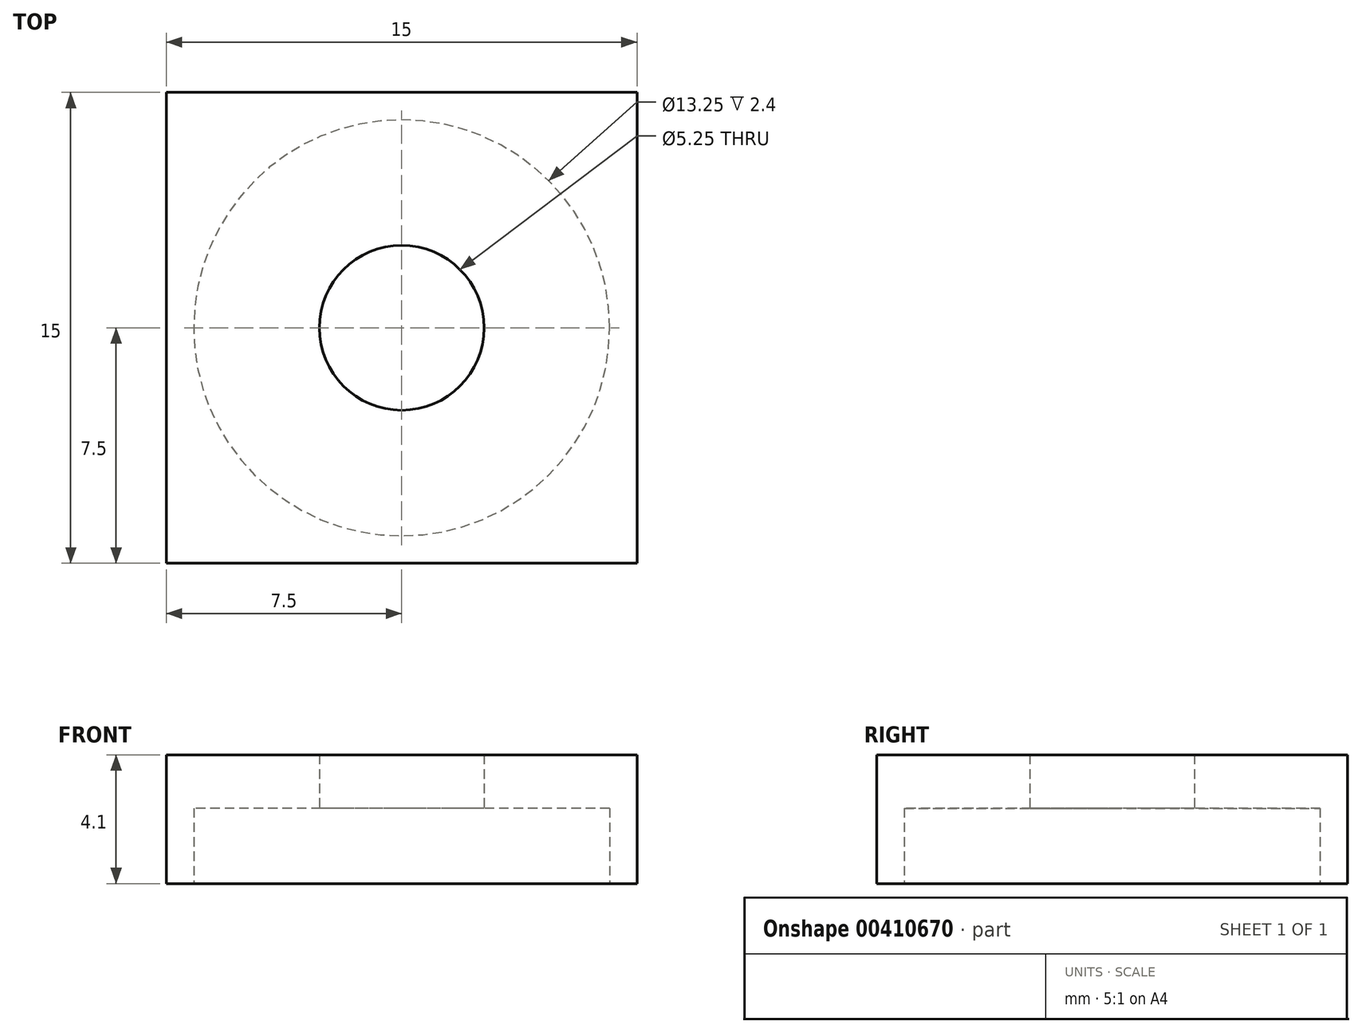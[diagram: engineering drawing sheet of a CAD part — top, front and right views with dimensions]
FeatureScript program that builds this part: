
annotation { "Feature Type Name" : "Feature", "Feature Type Description" : "" }
export const myFeature = defineFeature(function(context is Context, id is Id, definition is map)
    precondition{}
    {
        {
            var Q0;
            Q0=qCreatedBy(makeId("Top.planeOp"),FACE);
            var sketch = newSketch(context, id + "F0", { "sketchPlane" : qUnion([Q0])});
            skCircle(sketch, "E0", {"center": v(0, 0) * mm, "radius": 6.62 * mm});
            skLineSegment(sketch, "E1.bottom", {"start": v(-7.5, 7.5) * mm, "end": v(7.5, 7.5) * mm});
            skLineSegment(sketch, "E1.top", {"start": v(-7.5, -7.5) * mm, "end": v(7.5, -7.5) * mm});
            skLineSegment(sketch, "E1.left", {"start": v(-7.5, 7.5) * mm, "end": v(-7.5, -7.5) * mm});
            skLineSegment(sketch, "E1.right", {"start": v(7.5, 7.5) * mm, "end": v(7.5, -7.5) * mm});
            skSolve(sketch);
        }
        {
            var Q0;
            Q0 = qSketchRegion(id + "F0", true);
            extrude(context, id + "F1", {"entities" : qUnion([Q0]), "depth" : 2.4 * mm});
        }
        {
            var Q0;
            Q0=makeQuery(id+"F1.opExtrude","CAP_FACE",FACE,{"disambiguationData":[OSD([sQuery(id+"F0.wireOp",EDGE,"E0"),sQuery(id+"F0.wireOp",EDGE,"E1.bottom"),sQuery(id+"F0.wireOp",EDGE,"E1.top"),sQuery(id+"F0.wireOp",EDGE,"E1.left"),sQuery(id+"F0.wireOp",EDGE,"E1.right")])],"isStart":false});
            var sketch = newSketch(context, id + "F2", { "sketchPlane" : qUnion([Q0])});
            skLineSegment(sketch, "E2.0", {"start": v(-7.5, 7.5) * mm, "end": v(7.5, 7.5) * mm});
            skLineSegment(sketch, "E3.0", {"start": v(-7.5, 7.5) * mm, "end": v(-7.5, -7.5) * mm});
            skLineSegment(sketch, "E4.0", {"start": v(-7.5, -7.5) * mm, "end": v(7.5, -7.5) * mm});
            skLineSegment(sketch, "E5.0", {"start": v(7.5, 7.5) * mm, "end": v(7.5, -7.5) * mm});
            skSolve(sketch);
        }
        {
            var Q0;
            Q0 = qSketchRegion(id + "F2", true);
            extrude(context, id + "F3", {"entities" : qUnion([Q0]), "operationType" : NewBodyOperationType.ADD, "depth" : (6 - 2.3 - 2) * mm});
        }
        {
            var Q0;
            Q0=sQuery(id+"F0.wireOp",VERTEX,"E0.center");
            var Q1;
            Q1=makeQuery(id+"F1.opExtrude","SWEPT_BODY",BODY,{"disambiguationData":[OSD([sQuery(id+"F0.wireOp",EDGE,"E0"),sQuery(id+"F0.wireOp",EDGE,"E1.bottom"),sQuery(id+"F0.wireOp",EDGE,"E1.top"),sQuery(id+"F0.wireOp",EDGE,"E1.left"),sQuery(id+"F0.wireOp",EDGE,"E1.right")])]});
            hole(context, id + "F4", {"style" : HoleStyle.SIMPLE, "endStyle" : HoleEndStyle.THROUGH, "oppositeDirection" : true, "holeDiameter" : 5.25 * mm, "isTappedThrough" : true, "tappedDepth" : 38.4 * mm, "tapClearance" : 3, "locations" : qUnion([Q0]), "scope" : qUnion([Q1])});
        }
    });
